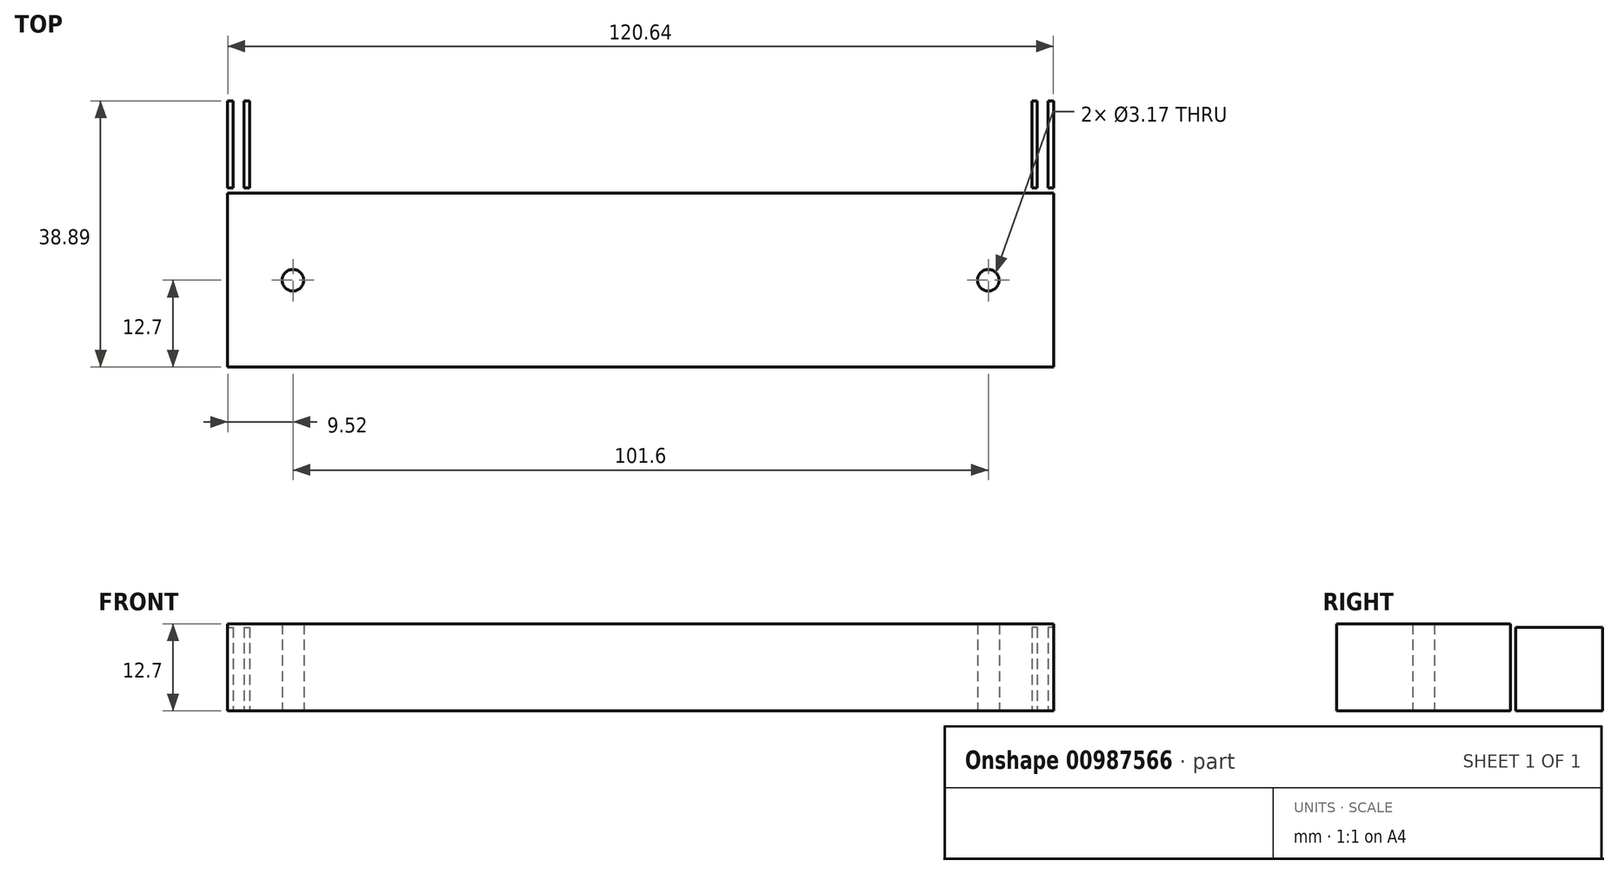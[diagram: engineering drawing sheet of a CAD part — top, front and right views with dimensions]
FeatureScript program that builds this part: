
annotation { "Feature Type Name" : "Feature", "Feature Type Description" : "" }
export const myFeature = defineFeature(function(context is Context, id is Id, definition is map)
    precondition{}
    {
        {
            var Q0;
            Q0=qCreatedBy(makeId("Top.planeOp"),FACE);
            var sketch = newSketch(context, id + "F0", { "sketchPlane" : qUnion([Q0])});
            skLineSegment(sketch, "E0.bottom", {"start": v(-60.33, 12.7) * mm, "end": v(60.33, 12.7) * mm});
            skLineSegment(sketch, "E0.top", {"start": v(-60.33, -12.7) * mm, "end": v(60.33, -12.7) * mm});
            skLineSegment(sketch, "E0.left", {"start": v(-60.32, 12.7) * mm, "end": v(-60.33, -12.7) * mm});
            skLineSegment(sketch, "E0.right", {"start": v(60.33, 12.7) * mm, "end": v(60.33, -12.7) * mm});
            skPoint(sketch, "E0.middle", {"position": v(0, 0) * mm});
            skLineSegment(sketch, "E1.bottom", {"start": v(-60.33, 13.5) * mm, "end": v(-59.53, 13.5) * mm});
            skLineSegment(sketch, "E1.top", {"start": v(-60.33, 26.2) * mm, "end": v(-59.53, 26.2) * mm});
            skLineSegment(sketch, "E1.left", {"start": v(-60.33, 13.5) * mm, "end": v(-60.33, 26.2) * mm});
            skLineSegment(sketch, "E1.right", {"start": v(-59.53, 13.5) * mm, "end": v(-59.53, 26.2) * mm});
            skLineSegment(sketch, "E2.bottom", {"start": v(-57.94, 13.5) * mm, "end": v(-57.15, 13.5) * mm});
            skLineSegment(sketch, "E2.top", {"start": v(-57.94, 26.2) * mm, "end": v(-57.15, 26.2) * mm});
            skLineSegment(sketch, "E2.left", {"start": v(-57.94, 13.5) * mm, "end": v(-57.94, 26.2) * mm});
            skLineSegment(sketch, "E2.right", {"start": v(-57.15, 13.5) * mm, "end": v(-57.15, 26.2) * mm});
            skLineSegment(sketch, "E3.bottom", {"start": v(60.33, 13.5) * mm, "end": v(59.53, 13.5) * mm});
            skLineSegment(sketch, "E3.top", {"start": v(60.32, 26.2) * mm, "end": v(59.53, 26.2) * mm});
            skLineSegment(sketch, "E3.left", {"start": v(60.33, 13.5) * mm, "end": v(60.33, 26.2) * mm});
            skLineSegment(sketch, "E3.right", {"start": v(59.53, 13.5) * mm, "end": v(59.53, 26.2) * mm});
            skLineSegment(sketch, "E4.bottom", {"start": v(57.94, 13.5) * mm, "end": v(57.15, 13.5) * mm});
            skLineSegment(sketch, "E4.top", {"start": v(57.94, 26.2) * mm, "end": v(57.15, 26.2) * mm});
            skLineSegment(sketch, "E4.left", {"start": v(57.94, 13.5) * mm, "end": v(57.94, 26.2) * mm});
            skLineSegment(sketch, "E4.right", {"start": v(57.15, 13.5) * mm, "end": v(57.15, 26.2) * mm});
            skCircle(sketch, "E5", {"center": v(-50.8, 0) * mm, "radius": 1.59 * mm});
            skCircle(sketch, "E6", {"center": v(50.8, 0) * mm, "radius": 1.59 * mm});
            skSolve(sketch);
        }
        {
            var Q0;
            Q0=makeQuery(id+"F0.imprint","IMPRINT",FACE,{"disambiguationData":[TD([[makeQuery(id+"F0.imprint","IMPRINT",EDGE,{"derivedFrom":sQuery(id+"F0.wireOp",EDGE,"E0.bottom")}),-1.0]])]});
            extrude(context, id + "F1", {"entities" : qUnion([Q0]), "depth" : 12.7 * mm, "offsetDistance" : 25.4 * mm});
        }
        {
            var Q0;
            Q0=makeQuery(id+"F0.imprint","IMPRINT",FACE,{"disambiguationData":[TD([[makeQuery(id+"F0.imprint","IMPRINT",EDGE,{"derivedFrom":sQuery(id+"F0.wireOp",EDGE,"E4.bottom")}),-1.0]])]});
            var Q1;
            Q1=makeQuery(id+"F0.imprint","IMPRINT",FACE,{"disambiguationData":[TD([[makeQuery(id+"F0.imprint","IMPRINT",EDGE,{"derivedFrom":sQuery(id+"F0.wireOp",EDGE,"E3.bottom")}),-1.0]])]});
            var Q2;
            Q2=makeQuery(id+"F0.imprint","IMPRINT",FACE,{"disambiguationData":[TD([[makeQuery(id+"F0.imprint","IMPRINT",EDGE,{"derivedFrom":sQuery(id+"F0.wireOp",EDGE,"E1.bottom")}),1.0]])]});
            var Q3;
            Q3=makeQuery(id+"F0.imprint","IMPRINT",FACE,{"disambiguationData":[TD([[makeQuery(id+"F0.imprint","IMPRINT",EDGE,{"derivedFrom":sQuery(id+"F0.wireOp",EDGE,"E2.bottom")}),1.0]])]});
            extrude(context, id + "F2", {"entities" : qUnion([Q0, Q1, Q2, Q3]), "depth" : 12.2 * mm, "offsetDistance" : 25.4 * mm});
        }
    });
